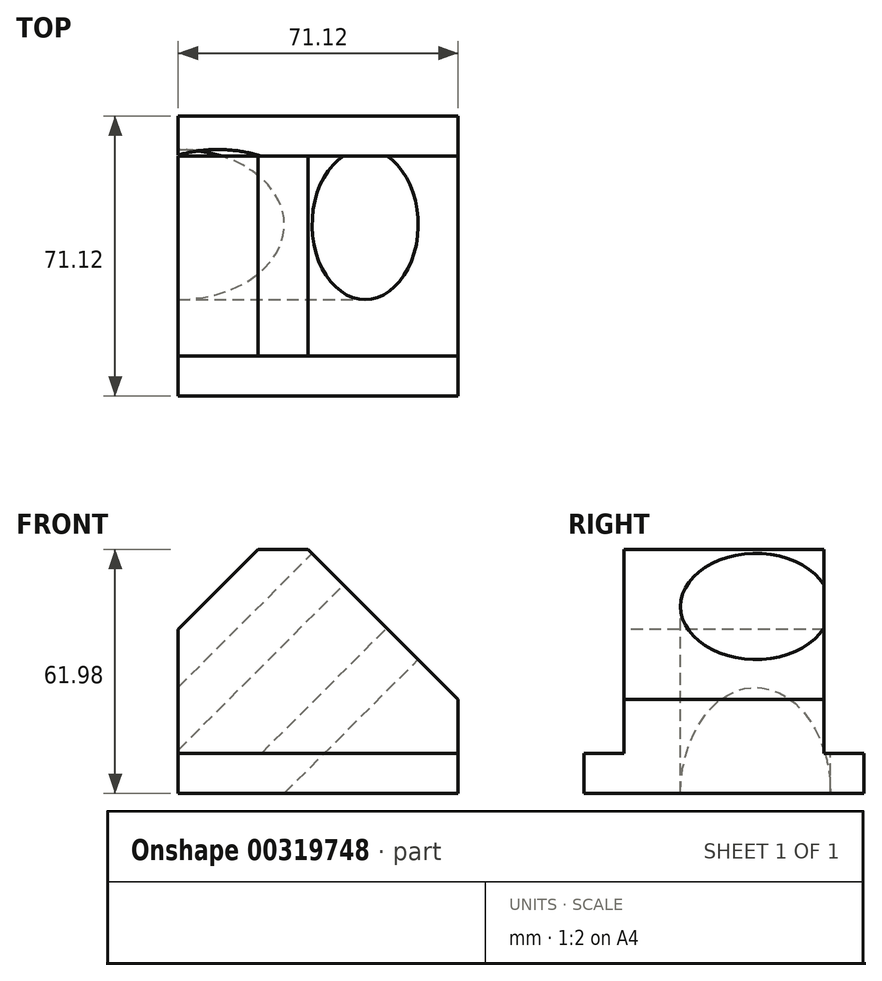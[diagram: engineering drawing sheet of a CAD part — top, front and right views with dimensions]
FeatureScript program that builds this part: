
annotation { "Feature Type Name" : "Feature", "Feature Type Description" : "" }
export const myFeature = defineFeature(function(context is Context, id is Id, definition is map)
    precondition{}
    {
        {
            var Q0;
            Q0=qCreatedBy(makeId("Front.planeOp"),FACE);
            var sketch = newSketch(context, id + "F0", { "sketchPlane" : qUnion([Q0])});
            skLineSegment(sketch, "E0.bottom", {"start": v(0, 0) * mm, "end": v(71.12, 0) * mm});
            skLineSegment(sketch, "E0.top", {"start": v(0, 61.98) * mm, "end": v(71.12, 61.98) * mm});
            skLineSegment(sketch, "E0.left", {"start": v(0, 0) * mm, "end": v(0, 61.98) * mm});
            skLineSegment(sketch, "E0.right", {"start": v(71.12, 0) * mm, "end": v(71.12, 61.98) * mm});
            skSolve(sketch);
        }
        {
            var Q0;
            Q0=makeQuery(id+"F0.imprint","IMPRINT",FACE,{"disambiguationData":[TD([[makeQuery(id+"F0.imprint","IMPRINT",EDGE,{"derivedFrom":sQuery(id+"F0.wireOp",EDGE,"E0.bottom")}),1.0]])]});
            extrude(context, id + "F1", {"entities" : qUnion([Q0]), "endBound" : BoundingType.SYMMETRIC, "depth" : 71.12 * mm});
        }
        {
            var Q0;
            Q0=makeQuery(id+"F1.opExtrude","SWEPT_FACE",FACE,{"disambiguationData":[OSD([sQuery(id+"F0.wireOp",EDGE,"E0.top")])]});
            var sketch = newSketch(context, id + "F2", { "sketchPlane" : qUnion([Q0])});
            skLineSegment(sketch, "E1.bottom", {"start": v(0, -35.56) * mm, "end": v(71.12, -35.56) * mm});
            skLineSegment(sketch, "E1.top", {"start": v(0, -25.4) * mm, "end": v(71.12, -25.4) * mm});
            skLineSegment(sketch, "E1.left", {"start": v(0, -35.56) * mm, "end": v(0, -25.4) * mm});
            skLineSegment(sketch, "E1.right", {"start": v(71.12, -35.56) * mm, "end": v(71.12, -25.4) * mm});
            skLineSegment(sketch, "E2.bottom", {"start": v(0, 35.56) * mm, "end": v(71.12, 35.56) * mm});
            skLineSegment(sketch, "E2.top", {"start": v(0, 25.4) * mm, "end": v(71.12, 25.4) * mm});
            skLineSegment(sketch, "E2.left", {"start": v(0, 35.56) * mm, "end": v(0, 25.4) * mm});
            skLineSegment(sketch, "E2.right", {"start": v(71.12, 35.56) * mm, "end": v(71.12, 25.4) * mm});
            skSolve(sketch);
        }
        {
            var Q0;
            Q0=makeQuery(id+"F2.imprint","IMPRINT",FACE,{"disambiguationData":[TD([[makeQuery(id+"F2.imprint","IMPRINT",EDGE,{"derivedFrom":sQuery(id+"F2.wireOp",EDGE,"E1.bottom")}),1.0]])]});
            var Q1;
            Q1=makeQuery(id+"F2.imprint","IMPRINT",FACE,{"disambiguationData":[TD([[makeQuery(id+"F2.imprint","IMPRINT",EDGE,{"derivedFrom":sQuery(id+"F2.wireOp",EDGE,"E2.bottom")}),-1.0]])]});
            extrude(context, id + "F3", {"entities" : qUnion([Q0, Q1]), "operationType" : NewBodyOperationType.REMOVE, "oppositeDirection" : true, "depth" : 51.82 * mm});
        }
        {
            var Q0;
            Q0=makeQuery(id+"F3.boolean.opBoolean","COPY",FACE,{"derivedFrom":makeQuery(id+"F3.opExtrude","SWEPT_FACE",FACE,{"disambiguationData":[OSD([sQuery(id+"F2.wireOp",EDGE,"E1.top")])]})});
            var sketch = newSketch(context, id + "F4", { "sketchPlane" : qUnion([Q0])});
            skLineSegment(sketch, "E3", {"start": v(0, 41.66) * mm, "end": v(20.32, 61.98) * mm});
            skLineSegment(sketch, "E4", {"start": v(33.02, 61.98) * mm, "end": v(71.12, 23.88) * mm});
            skSolve(sketch);
        }
        {
            var Q0;
            {var subQ0=sQuery(id+"F4.wireOp",EDGE,"E3");Q0=makeQuery(id+"F4.imprint","IMPRINT",FACE,{"disambiguationData":[TD([[makeQuery(id+"F4.imprint","IMPRINT",EDGE,{"derivedFrom":subQ0}),1.0]])]});}
            var Q1;
            {var subQ0=sQuery(id+"F4.wireOp",EDGE,"E4");Q1=makeQuery(id+"F4.imprint","IMPRINT",FACE,{"disambiguationData":[TD([[makeQuery(id+"F4.imprint","IMPRINT",EDGE,{"derivedFrom":subQ0}),1.0]])]});}
            extrude(context, id + "F5", {"entities" : qUnion([Q0, Q1]), "operationType" : NewBodyOperationType.REMOVE, "endBound" : BoundingType.THROUGH_ALL, "oppositeDirection" : true, "depth" : 25.4 * mm});
        }
        {
            var Q0;
            Q0=makeQuery(id+"F5.boolean.opBoolean","COPY",FACE,{"derivedFrom":makeQuery(id+"F5.opExtrude","SWEPT_FACE",FACE,{"disambiguationData":[OSD([sQuery(id+"F4.wireOp",EDGE,"E4")])]})});
            var sketch = newSketch(context, id + "F6", { "sketchPlane" : qUnion([Q0])});
            skCircle(sketch, "E5", {"center": v(8, 0) * mm, "radius": 19.05 * mm});
            skSolve(sketch);
        }
        {
            var Q0;
            Q0=makeQuery(id+"F6.imprint","IMPRINT",FACE,{"disambiguationData":[TD([[makeQuery(id+"F6.imprint","IMPRINT",EDGE,{"derivedFrom":sQuery(id+"F6.wireOp",EDGE,"E5")}),1.0]])]});
            extrude(context, id + "F7", {"entities" : qUnion([Q0]), "operationType" : NewBodyOperationType.REMOVE, "endBound" : BoundingType.THROUGH_ALL, "oppositeDirection" : true, "depth" : 25.4 * mm});
        }
    });
